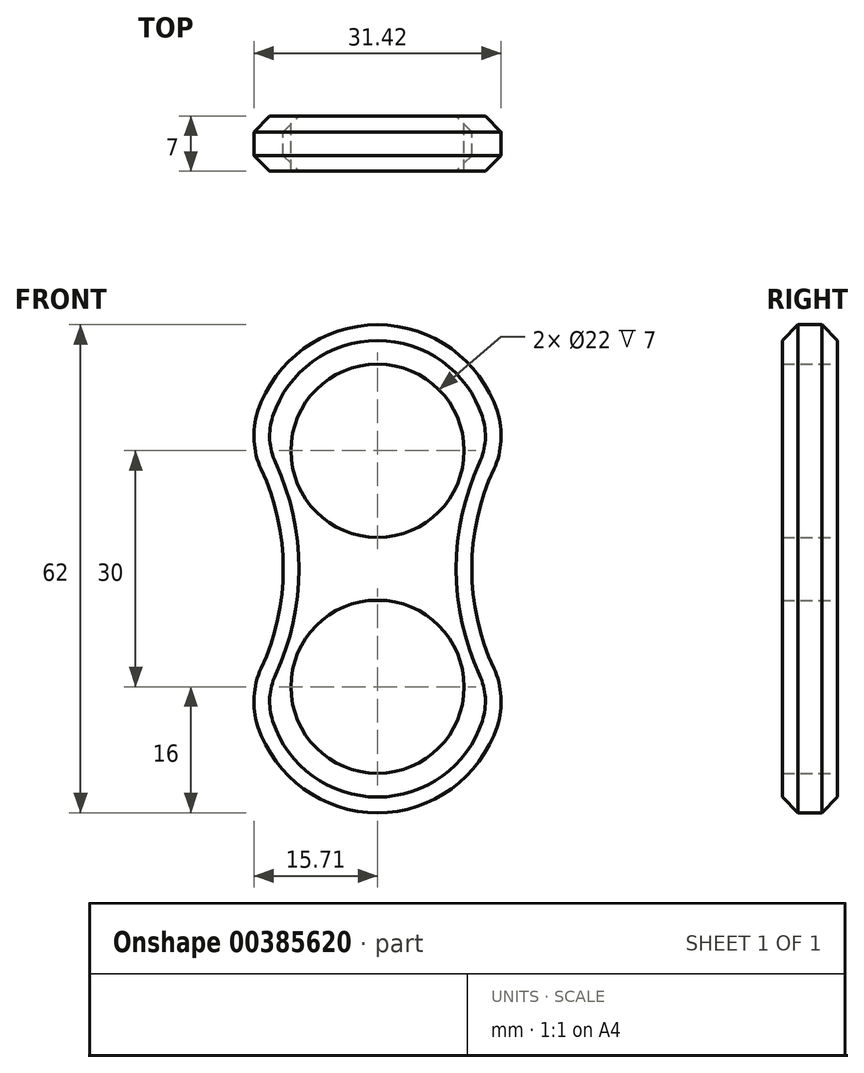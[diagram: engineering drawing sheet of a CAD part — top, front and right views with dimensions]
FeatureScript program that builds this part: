
annotation { "Feature Type Name" : "Feature", "Feature Type Description" : "" }
export const myFeature = defineFeature(function(context is Context, id is Id, definition is map)
    precondition{}
    {
        {
            var Q0;
            Q0=qCreatedBy(makeId("Front.planeOp"),FACE);
            var sketch = newSketch(context, id + "F0", { "sketchPlane" : qUnion([Q0])});
            skCircle(sketch, "E0", {"center": v(0, 0) * mm, "radius": 11 * mm});
            skCircle(sketch, "E1", {"center": v(0, 30) * mm, "radius": 11 * mm});
            skArc(sketch, "E2", {"start": v(15.22, 34.95) * mm, "mid": v(0, 46) * mm, "end": v(-15.22, 34.95) * mm});
            skArc(sketch, "E3", {"start": v(-15.22, -4.95) * mm, "mid": v(0, -16) * mm, "end": v(15.22, -4.95) * mm});
            skArc(sketch, "E4", {"start": v(-14.77, 2.36) * mm, "mid": v(-11.98, 15) * mm, "end": v(-14.77, 27.64) * mm});
            skArc(sketch, "E5", {"start": v(14.77, 27.64) * mm, "mid": v(11.98, 15) * mm, "end": v(14.77, 2.36) * mm});
            skPoint(sketch, "E6.visualSharp", {"position": v(-16, 30) * mm});
            skArc(sketch, "E6.filletArc", {"start": v(-15.22, 34.95) * mm, "mid": v(-15.69, 31.25) * mm, "end": v(-14.77, 27.64) * mm});
            skPoint(sketch, "E7.visualSharp", {"position": v(16, 30) * mm});
            skArc(sketch, "E7.filletArc", {"start": v(14.77, 27.64) * mm, "mid": v(15.69, 31.25) * mm, "end": v(15.22, 34.95) * mm});
            skPoint(sketch, "E8.visualSharp", {"position": v(16, 0) * mm});
            skArc(sketch, "E8.filletArc", {"start": v(15.22, -4.95) * mm, "mid": v(15.69, -1.25) * mm, "end": v(14.77, 2.36) * mm});
            skPoint(sketch, "E9.visualSharp", {"position": v(-16, 0) * mm});
            skArc(sketch, "E9.filletArc", {"start": v(-14.77, 2.36) * mm, "mid": v(-15.69, -1.25) * mm, "end": v(-15.22, -4.95) * mm});
            skSolve(sketch);
        }
        {
            var Q0;
            Q0=makeQuery(id+"F0.imprint","IMPRINT",FACE,{"disambiguationData":[TD([[makeQuery(id+"F0.imprint","IMPRINT",EDGE,{"derivedFrom":sQuery(id+"F0.wireOp",EDGE,"E0")}),-1.0]])]});
            extrude(context, id + "F1", {"entities" : qUnion([Q0]), "depth" : 7 * mm, "offsetDistance" : 25 * mm});
        }
        {
            var Q0;
            Q0=makeQuery(id+"F1.opExtrude","CAP_EDGE",EDGE,{"disambiguationData":[OSD([sQuery(id+"F0.wireOp",EDGE,"E2")])],"isStart":false});
            var Q1;
            Q1=makeQuery(id+"F1.opExtrude","CAP_EDGE",EDGE,{"disambiguationData":[OSD([sQuery(id+"F0.wireOp",EDGE,"E2")])],"isStart":true});
            chamfer(context, id + "F2", {"entities" : qUnion([Q0, Q1]), "width" : 2 * mm, "tangentPropagation" : true});
        }
    });
